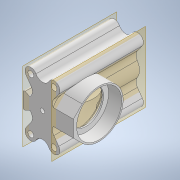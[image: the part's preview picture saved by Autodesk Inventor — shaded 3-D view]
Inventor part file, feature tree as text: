
AUTODESK INVENTOR PART (.ipt)
format: ipt  version: 2022 (Build 260153000, 153)  size: 467,456 bytes
history: native  units: mm
features: sketch x18, extrude x18, reference x11, other x6, plane x5, chamfer x3, projected_geometry x3, fillet x2, mirror x1
ambient origin geometry x8: Origin, YZ Plane, XZ Plane, XY Plane, X Axis, Y Axis, Z Axis, Center Point
bodies: Solid1 (feature_tree)
feature tree (67):
  sketch  "Sketch1"  dims[d0=0.3mm d1=2.0mm]
  plane  "Work Plane1"
  plane  "Work Plane6"
  extrude  "Extrusion1"  Depth=2.0mm
  extrude  "Extrusion2"  Depth=10.0mm TaperAngle=0.0deg
  extrude  "Extrusion3"  Depth=0.3mm TaperAngle=0.0deg
  extrude  "Extrusion4"  Depth=0.3mm TaperAngle=0.0deg
  extrude  "Extrusion5"  Depth=4.0mm
  fillet  "Fillet1"  Radius=4.0mm
  extrude  "Extrusion6"  Depth=10.0mm
  mirror  "Mirror1"
  extrude  "Extrusion7"  TaperAngle=0.0deg  [1 undecoded]
  chamfer  "Chamfer1"  Distance=7.3mm Angle=45.0deg
  plane  "Work Plane4"
  extrude  "Extrusion10"  TaperAngle=0.0deg  [1 undecoded]
  plane  "Work Plane5"
  extrude  "Extrusion11"  Depth=10.0mm TaperAngle=0.0deg
  extrude  "Extrusion12"  Depth=1.0mm TaperAngle=0.0deg
  chamfer  "Chamfer2"  Distance=1.0mm Angle=45.0deg
  extrude  "Extrusion13"  Depth=10.0mm TaperAngle=0.0deg
  extrude  "Extrusion16"  Depth=1.0mm TaperAngle=0.0deg
  extrude  "Extrusion18"  Depth=10.0mm
  extrude  "Extrusion19"  Depth=3.5mm
  extrude  "Extrusion21"  Depth=1.0mm TaperAngle=45.0deg
  extrude  "Extrusion22"  Depth=1.0mm TaperAngle=0.0deg
  chamfer  "Chamfer3"  Distance=9.0mm
  extrude  "Extrusion23"  Depth=1.0mm
  extrude  "Extrusion24"  Depth=1.0mm
  fillet  "Fillet2"  Radius=0.5mm
  reference  "Reference1"
  reference  "Reference2"
  reference  "Reference3"
  sketch  "Sketch2"  dims[d2=10.0mm d3=0.0mm d5=3.0mm d6=0.0mm]
  sketch  "Sketch3"  dims[d7=2.0mm d8=0.0mm d10=0.3mm d11=0.0mm]
  projected_geometry  "Projected Loop1"
  sketch  "Sketch5"  dims[d12=2.0mm d13=0.3mm d14=0.0mm]
  projected_geometry  "Projected Loop2"
  sketch  "Sketch6"  dims[d15=5.0mm d16=4.0mm d17=4.0mm]
  reference  "Reference6"
  reference  "Reference7"
  sketch  "Sketch7"  dims[d18=10.0mm d19=0.0mm d22=0.3mm]
  reference  "Reference8"
  reference  "Reference9"
  reference  "Reference10"
  reference  "Reference11"
  plane  "Work Plane2"
  other  "Work Point1"
  sketch  "Sketch9"  dims[d23=31.0mm d24=0.0mm d25=0.0mm d26=7.3mm d27=2.0mm d28=45.0deg]
  sketch  "Sketch12"  dims[d36=2.0mm d37=0.0mm d38=0.0mm]
  sketch  "Sketch13"  dims[d39=1.0mm d40=10.0mm d41=0.0mm]
  sketch  "Sketch14"  dims[d42=1.0mm d43=1.0mm d44=0.0mm d45=1.0mm d46=2.0mm d47=45.0deg]
  projected_geometry  "Projected Loop3"
  sketch  "Sketch15"  dims[d48=3.0mm d49=0.0mm d56=10.0mm d57=0.0mm]
  sketch  "Sketch19"  dims[d69=1.0mm d70=3.0mm d71=2.0mm d72=0.0mm d73=0.0mm]
  reference  "Reference13"
  sketch  "Sketch22"  dims[d74=10.0mm d75=0.0mm d79=3.0mm]
  sketch  "Sketch23"  dims[d80=0.0mm d81=0.0mm d82=3.5mm]
  sketch  "Sketch25"  dims[d83=1.0mm d84=0.0mm d85=3.5mm d86=2.0mm d87=45.0deg]
  reference  "Reference14"
  sketch  "Sketch26"  dims[d88=1.0mm d89=9.0mm d90=0.0mm]
  sketch  "Sketch27"  dims[d91=45.0deg d92=9.0mm d93=0.0mm]
  sketch  "Sketch28"  dims[d94=1.0mm d53=0.5mm d54=0.872665mm d55=0.5mm d67=0.5mm d68=0.872665mm d76=0.5mm d77=0.872665mm]
  other  "<userpath>\OneDrive - Imperial College London\ROBOICP MK2\solids feeder assembly.iam"
  other  "solids feeder assembly.iam"
  other  "shaft endcap:1"
  other  "Screw Shaft:1"
  other  "smol stepper:1"
note: 2 required parameter values undecoded (feature->parameter linkage not recoverable at this tier; creation-order binding heuristic only, values carry confidence <= 0.55)
